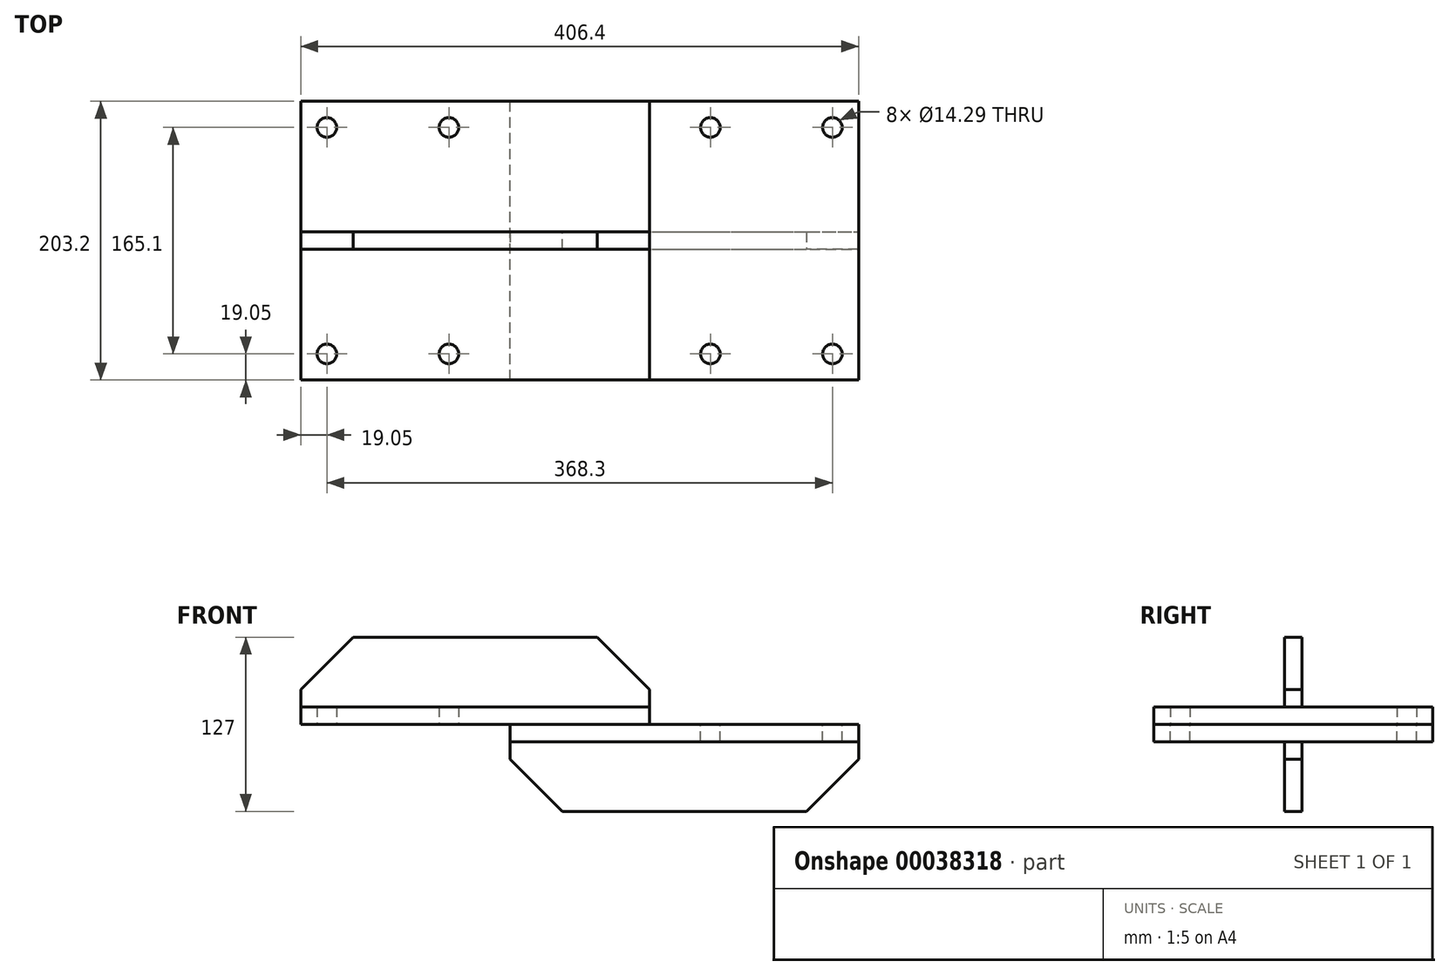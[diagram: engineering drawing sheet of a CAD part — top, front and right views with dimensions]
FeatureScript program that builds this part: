
annotation { "Feature Type Name" : "Feature", "Feature Type Description" : "" }
export const myFeature = defineFeature(function(context is Context, id is Id, definition is map)
    precondition{}
    {
        {
            var Q0;
            Q0=qCreatedBy(makeId("Top.planeOp"),FACE);
            var sketch = newSketch(context, id + "F0", { "sketchPlane" : qUnion([Q0])});
            skLineSegment(sketch, "E0", {"start": v(0, 106.75) * mm, "end": v(0, -105.6) * mm, "construction": true});
            skLineSegment(sketch, "E1.0", {"start": v(-203.2, 106.75) * mm, "end": v(-203.2, -105.6) * mm, "construction": true});
            skLineSegment(sketch, "E2.MirrorCS", {"start": v(203.2, 106.75) * mm, "end": v(203.2, -105.6) * mm, "construction": true});
            skLineSegment(sketch, "E3", {"start": v(-283.64, 0) * mm, "end": v(308.6, 0) * mm, "construction": true});
            skLineSegment(sketch, "E4.0", {"start": v(-283.64, -101.6) * mm, "end": v(308.6, -101.6) * mm, "construction": true});
            skLineSegment(sketch, "E5.bottom", {"start": v(-203.2, -101.6) * mm, "end": v(50.8, -101.6) * mm});
            skLineSegment(sketch, "E5.top", {"start": v(-203.2, 101.6) * mm, "end": v(50.8, 101.6) * mm});
            skLineSegment(sketch, "E5.left", {"start": v(-203.2, -101.6) * mm, "end": v(-203.2, 101.6) * mm});
            skLineSegment(sketch, "E5.right", {"start": v(50.8, -101.6) * mm, "end": v(50.8, 101.6) * mm});
            skLineSegment(sketch, "E6.0", {"start": v(-139.7, -101.6) * mm, "end": v(-139.7, 101.6) * mm, "construction": true});
            skLineSegment(sketch, "E7.0", {"start": v(-184.15, -101.6) * mm, "end": v(-184.15, 101.6) * mm, "construction": true});
            skLineSegment(sketch, "E8.0", {"start": v(-283.64, -82.55) * mm, "end": v(308.6, -82.55) * mm, "construction": true});
            skCircle(sketch, "E9", {"center": v(-184.15, -82.55) * mm, "radius": 7.14 * mm});
            skCircle(sketch, "E10.MirrorC", {"center": v(-95.25, -82.55) * mm, "radius": 7.14 * mm});
            skCircle(sketch, "E11.MirrorC", {"center": v(-95.25, 82.55) * mm, "radius": 7.14 * mm});
            skCircle(sketch, "E12.MirrorC", {"center": v(-184.15, 82.55) * mm, "radius": 7.14 * mm});
            skSolve(sketch);
        }
        {
            var Q0;
            Q0=makeQuery(id+"F0.imprint","IMPRINT",FACE,{"disambiguationData":[TD([[makeQuery(id+"F0.imprint","IMPRINT",EDGE,{"derivedFrom":sQuery(id+"F0.wireOp",EDGE,"E5.bottom")}),1.0]])]});
            extrude(context, id + "F1", {"entities" : qUnion([Q0]), "depth" : 12.7 * mm});
        }
        {
            var Q0;
            Q0=makeQuery(id+"F1.opExtrude","CAP_FACE",FACE,{"disambiguationData":[OSD([sQuery(id+"F0.wireOp",EDGE,"E5.bottom"),sQuery(id+"F0.wireOp",EDGE,"E5.top"),sQuery(id+"F0.wireOp",EDGE,"E5.left"),sQuery(id+"F0.wireOp",EDGE,"E5.right"),sQuery(id+"F0.wireOp",EDGE,"E9"),sQuery(id+"F0.wireOp",EDGE,"E10.MirrorC"),sQuery(id+"F0.wireOp",EDGE,"E11.MirrorC"),sQuery(id+"F0.wireOp",EDGE,"E12.MirrorC")])],"isStart":true});
            var sketch = newSketch(context, id + "F2", { "sketchPlane" : qUnion([Q0])});
            skLineSegment(sketch, "E13.0", {"start": v(-283.64, 101.6) * mm, "end": v(308.6, 101.6) * mm, "construction": true});
            skLineSegment(sketch, "E14.0", {"start": v(203.2, -106.75) * mm, "end": v(203.2, 105.6) * mm, "construction": true});
            skLineSegment(sketch, "E15.bottom", {"start": v(203.2, 101.6) * mm, "end": v(-50.8, 101.6) * mm});
            skLineSegment(sketch, "E15.top", {"start": v(203.2, -101.6) * mm, "end": v(-50.8, -101.6) * mm});
            skLineSegment(sketch, "E15.left", {"start": v(203.2, 101.6) * mm, "end": v(203.2, -101.6) * mm});
            skLineSegment(sketch, "E15.right", {"start": v(-50.8, 101.6) * mm, "end": v(-50.8, -101.6) * mm});
            skLineSegment(sketch, "E16.0", {"start": v(139.7, 101.6) * mm, "end": v(139.7, -101.6) * mm, "construction": true});
            skLineSegment(sketch, "E17.0", {"start": v(184.15, 101.6) * mm, "end": v(184.15, -101.6) * mm, "construction": true});
            skLineSegment(sketch, "E18.0", {"start": v(-283.64, 82.55) * mm, "end": v(308.6, 82.55) * mm, "construction": true});
            skCircle(sketch, "E19", {"center": v(184.15, 82.55) * mm, "radius": 7.14 * mm});
            skCircle(sketch, "E20.MirrorC", {"center": v(95.25, 82.55) * mm, "radius": 7.14 * mm});
            skCircle(sketch, "E21.MirrorC", {"center": v(95.25, -82.55) * mm, "radius": 7.14 * mm});
            skCircle(sketch, "E22.MirrorC", {"center": v(184.15, -82.55) * mm, "radius": 7.14 * mm});
            skSolve(sketch);
        }
        {
            var Q0;
            Q0 = qSketchRegion(id + "F2", true);
            extrude(context, id + "F3", {"entities" : qUnion([Q0]), "depth" : 12.7 * mm});
        }
        {
            var Q0;
            Q0=makeQuery(id+"F1.opExtrude","CAP_FACE",FACE,{"disambiguationData":[OSD([sQuery(id+"F0.wireOp",EDGE,"E5.bottom"),sQuery(id+"F0.wireOp",EDGE,"E5.top"),sQuery(id+"F0.wireOp",EDGE,"E5.left"),sQuery(id+"F0.wireOp",EDGE,"E5.right"),sQuery(id+"F0.wireOp",EDGE,"E9"),sQuery(id+"F0.wireOp",EDGE,"E10.MirrorC"),sQuery(id+"F0.wireOp",EDGE,"E11.MirrorC"),sQuery(id+"F0.wireOp",EDGE,"E12.MirrorC")])],"isStart":false});
            var sketch = newSketch(context, id + "F4", { "sketchPlane" : qUnion([Q0])});
            skLineSegment(sketch, "E23.0", {"start": v(-283.64, 0) * mm, "end": v(308.6, 0) * mm, "construction": true});
            skLineSegment(sketch, "E24.0", {"start": v(-203.2, -6.35) * mm, "end": v(50.8, -6.35) * mm});
            skLineSegment(sketch, "E25.0", {"start": v(-203.2, -6.35) * mm, "end": v(-203.2, 6.35) * mm});
            skLineSegment(sketch, "E26.0", {"start": v(50.8, -6.35) * mm, "end": v(50.8, 6.35) * mm});
            skLineSegment(sketch, "E27.MirrorCS", {"start": v(-203.2, 6.35) * mm, "end": v(50.8, 6.35) * mm});
            skPoint(sketch, "E28.orphan", {"position": v(-283.64, 6.35) * mm});
            skPoint(sketch, "E29.orphan", {"position": v(-283.64, -6.35) * mm});
            skPoint(sketch, "E30.orphan", {"position": v(308.6, 6.35) * mm});
            skPoint(sketch, "E31.orphan", {"position": v(308.6, -6.35) * mm});
            skPoint(sketch, "E32.orphan", {"position": v(50.8, 101.6) * mm});
            skPoint(sketch, "E33.orphan", {"position": v(50.8, -101.6) * mm});
            skPoint(sketch, "E34.orphan", {"position": v(-203.2, -101.6) * mm});
            skPoint(sketch, "E35.orphan", {"position": v(-203.2, 101.6) * mm});
            skSolve(sketch);
        }
        {
            var Q0;
            Q0 = qSketchRegion(id + "F4", true);
            extrude(context, id + "F5", {"entities" : qUnion([Q0]), "depth" : 50.8 * mm});
        }
        {
            var Q0;
            Q0=makeQuery(id+"F5.opExtrude","CAP_EDGE",EDGE,{"disambiguationData":[OSD([sQuery(id+"F4.wireOp",EDGE,"E25.0")])],"isStart":false});
            var Q1;
            Q1=makeQuery(id+"F5.opExtrude","CAP_EDGE",EDGE,{"disambiguationData":[OSD([sQuery(id+"F4.wireOp",EDGE,"E26.0")])],"isStart":false});
            chamfer(context, id + "F6", {"entities" : qUnion([Q0, Q1]), "width" : 38.1 * mm, "tangentPropagation" : true});
        }
        {
            var Q0;
            Q0=makeQuery(id+"F3.opExtrude","CAP_FACE",FACE,{"disambiguationData":[OSD([sQuery(id+"F2.wireOp",EDGE,"E15.bottom"),sQuery(id+"F2.wireOp",EDGE,"E15.top"),sQuery(id+"F2.wireOp",EDGE,"E15.left"),sQuery(id+"F2.wireOp",EDGE,"E15.right"),sQuery(id+"F2.wireOp",EDGE,"E19"),sQuery(id+"F2.wireOp",EDGE,"E20.MirrorC"),sQuery(id+"F2.wireOp",EDGE,"E21.MirrorC"),sQuery(id+"F2.wireOp",EDGE,"E22.MirrorC")])],"isStart":false});
            var sketch = newSketch(context, id + "F7", { "sketchPlane" : qUnion([Q0])});
            skLineSegment(sketch, "E36.0", {"start": v(-283.64, 0) * mm, "end": v(308.6, 0) * mm, "construction": true});
            skLineSegment(sketch, "E37.0", {"start": v(-50.8, 101.6) * mm, "end": v(-50.8, -101.6) * mm});
            skLineSegment(sketch, "E38.0", {"start": v(203.2, -106.75) * mm, "end": v(203.2, 105.6) * mm});
            skLineSegment(sketch, "E39.0", {"start": v(-283.64, -6.35) * mm, "end": v(308.6, -6.35) * mm});
            skLineSegment(sketch, "E40.MirrorCS", {"start": v(-283.64, 6.35) * mm, "end": v(308.6, 6.35) * mm});
            skSolve(sketch);
        }
        {
            var Q0;
            {var subQ0=sQuery(id+"F7.wireOp",EDGE,"E40.MirrorCS");var subQ3=sQuery(id+"F7.wireOp",EDGE,"E37.0");var subQ4=makeQuery(id+"F7.imprint","INTERSECT",VERTEX,{"derivedFrom":[subQ3,subQ0]});Q0=makeQuery(id+"F7.imprint","IMPRINT",FACE,{"disambiguationData":[TD([[makeQuery(id+"F7.imprint","IMPRINT",EDGE,{"disambiguationData":[TD([[subQ4,-1.0]])],"derivedFrom":subQ3}),1.0]])]});}
            extrude(context, id + "F8", {"entities" : qUnion([Q0]), "depth" : 50.8 * mm});
        }
        {
            var Q0;
            Q0=makeQuery(id+"F8.opExtrude","CAP_EDGE",EDGE,{"disambiguationData":[OSD([sQuery(id+"F7.wireOp",EDGE,"E38.0")])],"isStart":false});
            var Q1;
            Q1=makeQuery(id+"F8.opExtrude","CAP_EDGE",EDGE,{"disambiguationData":[OSD([sQuery(id+"F7.wireOp",EDGE,"E37.0")])],"isStart":false});
            chamfer(context, id + "F9", {"entities" : qUnion([Q0, Q1]), "width" : 38.1 * mm, "tangentPropagation" : true});
        }
    });
